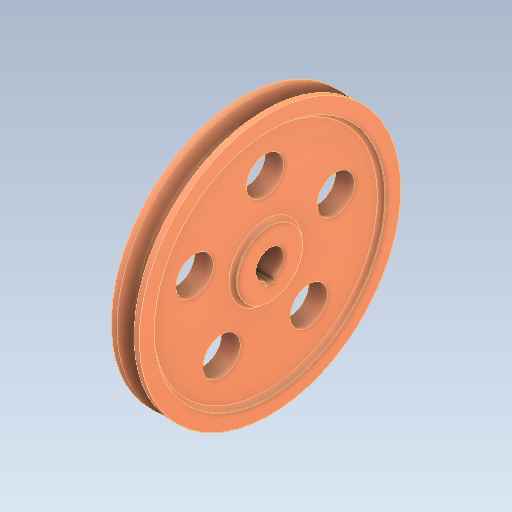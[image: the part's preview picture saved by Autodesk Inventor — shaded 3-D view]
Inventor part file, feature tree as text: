
AUTODESK INVENTOR PART (.ipt)
format: ipt  version: 2021 (Build 250183000, 183)  size: 220,160 bytes
history: mixed  units: mm
features: other x1, extrude x1, imported_body x1
ambient origin geometry x8: Origin, YZ Plane, XZ Plane, XY Plane, X Axis, Y Axis, Z Axis, Center Point
bodies: Body1 (imported_parasolid)
feature tree (3):
  other  "Sólido1"
  extrude  "Extrude2"  [1 undecoded]
  imported_body  NMx_Import_Brep_tag  [imported B-rep: ~28 faces, bbox_mm=[15.0, 77.786278, 104.714327]]
note: 1 required parameter value undecoded (feature->parameter linkage not recoverable at this tier; creation-order binding heuristic only, values carry confidence <= 0.55)
